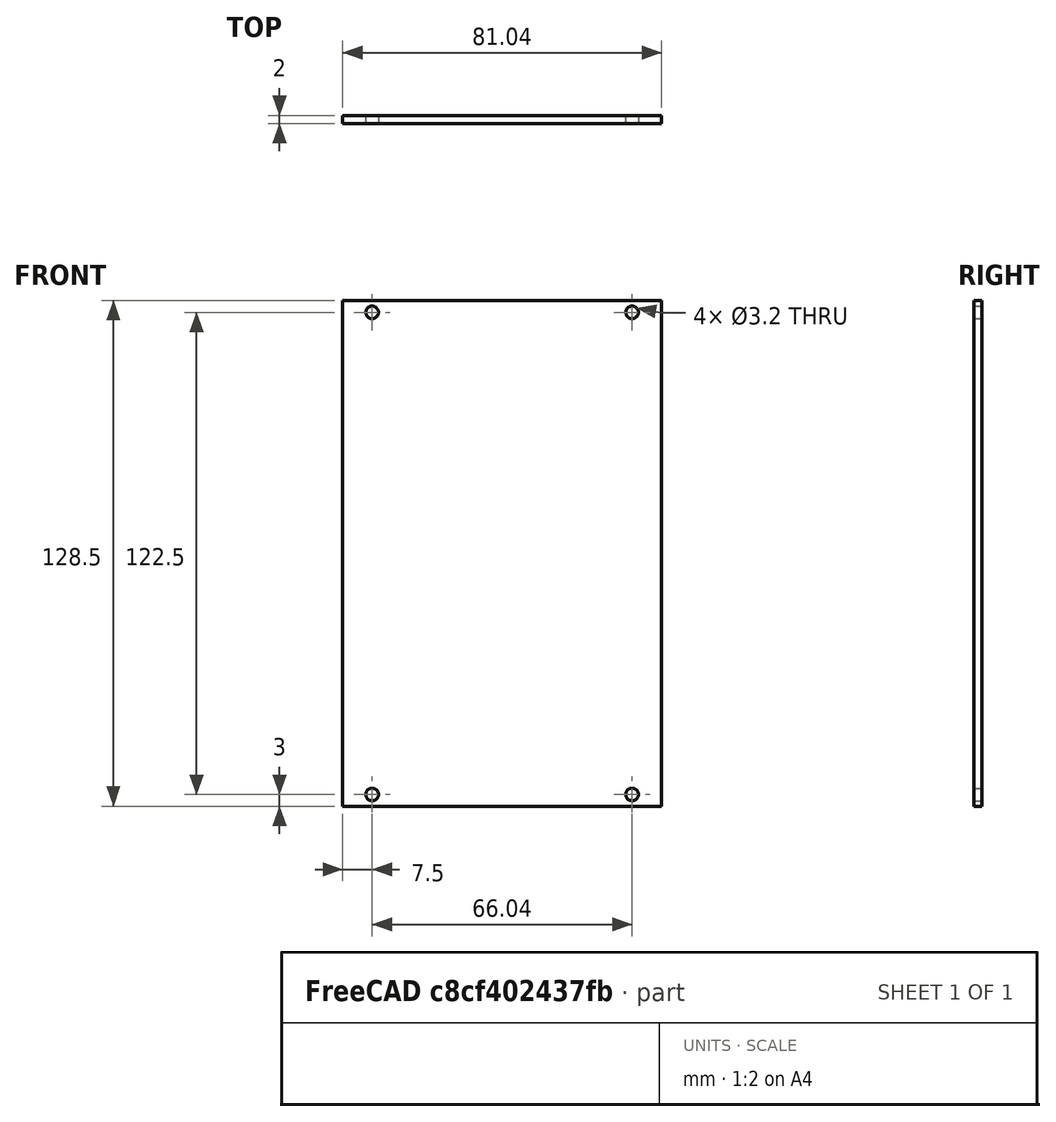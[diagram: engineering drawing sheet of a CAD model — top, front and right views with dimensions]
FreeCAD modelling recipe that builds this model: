
FCSTD DOCUMENT  (FreeCAD 1.0R38641 +468 (Git))
Label: 16hp_plate
License: All rights reserved
LicenseURL: https://en.wikipedia.org/wiki/All_rights_reserved
objects: Sketcher::SketchObject×1, PartDesign::Pad×1, PartDesign::Body×1, App::VarSet×1
note: 6 computed .brp shape members not serialized (recipe doc carries the construction recipe); baked Part::Feature solids carry a one-line shape summary decoded from their .brp
EXTERNAL_REF file=plate_dims.FCStd obj=VarSet

FEATURE [Sketcher::SketchObject] Sketch
  ArcFitTolerance = 1e-06
  AttachmentSupport = -> [XZ_Plane]
  FullyConstrained = true
  MakeInternals = false
  MapMode = 5
  Placement = pos=(0,0,0) rot=(1,0,0;1.5708rad)
  expr: Constraints[39] = <<plate_dims>>#VarSet.HoleOffsetY
  expr: Constraints[40] = <<plate_dims>>#VarSet.HoleOffsetX
  expr: Constraints[48] = <<plate_dims>>#VarSet.HoleDiameter
  expr: Constraints[49] = <<plate_dims>>#VarSet.PlateHeight
  expr: Constraints[52] = <<plate_dims>>#VarSet.HoleSpacing * (VarSet.PlateWidthHP - 3)
  sketch-geometry (20):
    g0: LineSegment StartX=-40.52 StartY=64.25 StartZ=0 EndX=-40.52 EndY=-64.25 EndZ=0
    g1: LineSegment StartX=-40.52 StartY=-64.25 StartZ=0 EndX=40.52 EndY=-64.25 EndZ=0
    g2: LineSegment StartX=40.52 StartY=-64.25 StartZ=0 EndX=40.52 EndY=64.25 EndZ=0
    g3: LineSegment StartX=40.52 StartY=64.25 StartZ=0 EndX=-40.52 EndY=64.25 EndZ=0
    g4: LineSegment [constr] StartX=33.02 StartY=61.25 StartZ=0 EndX=40.52 EndY=61.25 EndZ=0
    g5: LineSegment [constr] StartX=33.02 StartY=64.25 StartZ=0 EndX=33.02 EndY=61.25 EndZ=0
    g6: LineSegment [constr] StartX=33.02 StartY=61.25 StartZ=0 EndX=33.02 EndY=-61.25 EndZ=0
    g7: LineSegment [constr] StartX=33.02 StartY=-61.25 StartZ=0 EndX=33.02 EndY=-64.25 EndZ=0
    g8: LineSegment [constr] StartX=33.02 StartY=-61.25 StartZ=0 EndX=40.52 EndY=-61.25 EndZ=0
    g9: LineSegment [constr] StartX=-33.02 StartY=-61.25 StartZ=0 EndX=-33.02 EndY=-64.25 EndZ=0
    g10: LineSegment [constr] StartX=-40.52 StartY=-61.25 StartZ=0 EndX=-33.02 EndY=-61.25 EndZ=0
    g11: LineSegment [constr] StartX=-33.02 StartY=-61.25 StartZ=0 EndX=33.02 EndY=-61.25 EndZ=0
    g12: LineSegment [constr] StartX=-40.52 StartY=61.25 StartZ=0 EndX=-33.02 EndY=61.25 EndZ=0
    g13: LineSegment [constr] StartX=-33.02 StartY=61.25 StartZ=0 EndX=33.02 EndY=61.25 EndZ=0
    g14: LineSegment [constr] StartX=-33.02 StartY=64.25 StartZ=0 EndX=-33.02 EndY=61.25 EndZ=0
    g15: LineSegment [constr] StartX=-33.02 StartY=61.25 StartZ=0 EndX=-33.02 EndY=-61.25 EndZ=0
    g16: Circle CenterX=-33.02 CenterY=61.25 CenterZ=0 NormalX=0 NormalY=0 NormalZ=1 AngleXU=0 Radius=1.6
    g17: Circle CenterX=33.02 CenterY=61.25 CenterZ=0 NormalX=0 NormalY=0 NormalZ=1 AngleXU=0 Radius=1.6
    g18: Circle CenterX=33.02 CenterY=-61.25 CenterZ=0 NormalX=0 NormalY=0 NormalZ=1 AngleXU=0 Radius=1.6
    g19: Circle CenterX=-33.02 CenterY=-61.25 CenterZ=0 NormalX=0 NormalY=0 NormalZ=1 AngleXU=0 Radius=1.6
  constraints (58):
    c: Coincident(g0,g1)
    c: Coincident(g1,g2)
    c: Coincident(g2,g3)
    c: Coincident(g3,g0)
    c: Vertical(g2)
    c: Horizontal(g1)
    c: PointOnObject(g14,g3)
    c: PointOnObject(g9,g1)
    c: PointOnObject(g12,g0)
    c: PointOnObject(g4,g2)
    c: PointOnObject(g10,g0)
    c: PointOnObject(g8,g2)
    c: PointOnObject(g5,g3)
    c: PointOnObject(g7,g1)
    c: Coincident(g13,g4)
    c: Horizontal(g4)
    c: Coincident(g5,g6)
    c: Vertical(g5)
    c: Coincident(g6,g7)
    c: Vertical(g6)
    c: Vertical(g7)
    c: Coincident(g11,g8)
    c: Horizontal(g8)
    c: Coincident(g15,g9)
    c: Vertical(g9)
    c: Coincident(g10,g11)
    c: Horizontal(g10)
    c: Horizontal(g11)
    c: Coincident(g12,g13)
    c: Horizontal(g12)
    c: Horizontal(g13)
    c: Coincident(g14,g15)
    c: Vertical(g14)
    c: Vertical(g15)
    c: Coincident(g12,g14)
    c: Coincident(g9,g10)
    c: Coincident(g8,g6)
    c: Coincident(g4,g5)
    c: Equal(g9,g14)
    c: Distance(g9,g9) = 3
    c: Distance(g10,g10) = 7.5
    c: Coincident(g16,g12)
    c: Coincident(g17,g4)
    c: Coincident(g18,g6)
    c: Coincident(g19,g9)
    c: Equal(g19,g18)
    c: Equal(g18,g17)
    c: Equal(g17,g16)
    c: Diameter(g16) = 3.2
    c: DistanceY(g0,g0) = 128.5
    c: Distance(g12,g9) = 125.5
    c: Distance(g14,g14) = 3
    c: Distance(g11,g11) = 66.04
    c: Distance(g1,g1) = 81.04
    c: Symmetric(g0,g2,g-2)
    c: Symmetric(g0,g0,g-1)
    c: Distance(g8,g8) = 7.5
    c: Equal(g8,g10)
FEATURE [PartDesign::Pad] Pad
  Direction = (0,-1,2e-16)
  Length = 2
  Length2 = 10
  Placement = pos=(0,0,0) rot=(1,0,0;1.5708rad)
  Profile = -> Sketch
  ReferenceAxis = -> Sketch [N_Axis]
  Refine = true
  Suppressed = false
  Type = 0
FEATURE [PartDesign::Body] Body  label="16HpPlate"
  AllowCompound = false
  Group = -> [Sketch,Pad]
  Origin = -> Origin
  Tip = -> Pad
FEATURE [App::VarSet] VarSet
  PlateWidthHP = 16
